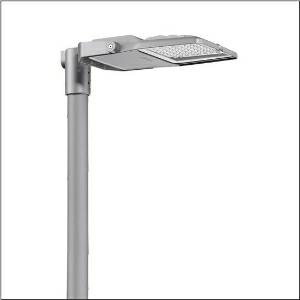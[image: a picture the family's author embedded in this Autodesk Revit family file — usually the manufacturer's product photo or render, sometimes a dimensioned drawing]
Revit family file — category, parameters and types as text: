
# Revit family: floodlight_fl_21_mini___pl43_5xa7776b4a3a_9af8
name_source: partatom
category: Lighting Fixtures
units: mm (PartAtom-declared; Revit-internal decimal feet)

## family parameters
Cut with Voids When Loaded = No
Host = Face
Light Source = No
Part Type = Normal
Room Calculation Point = No
Round Connector Dimension = Use Diameter
Shared = No

## types (1)
- --- (1 x LED, 6650 lm, 45.7 W, 4000K)
    Apparent Load = 46 VA
    CIE Flux Codes = 27 78 99 100 100
    Color Rendering = 70
    Color Temperature = 4000K
    Default Elevation = 1800 mm
    Description = Floodlight FL 21 mini, floodlight, primary light control with lens, of PMMA, primary optical cover: protective disc, of toughened safety glass, transparent, light distribution: PL43, light emission: direct distribution, installation type: surface-mounted, LED, High Power LED, rated luminous flux: 6.650lm, luminous efficacy: 146lm/W, light colour: 740, colour temperature: 4000K, control gear: D4iSmart Interface (Zhaga), control: overheat protection, constant luminous flux control, time-dependent luminous flux control, flexible luminous flux parameterisation, pre-setting: logarithmic dimming characteristic, with terminal, 6-pole, mains connection: 220..240V, AC, 50/60Hz, start of lifetime: 46W, end of service life: 48W, reduction: 22W, mast bracket, of diecast aluminium, powder-coated, SITECO metallic grey (DB 702S), corrosivity category C5 mid according to DIN EN ISO 12944, suitable for swimming pools, chlorine-resistant, sealing non-destructively replaceable, mast bracket, of steel, galvanised, powder-coated, SITECO metallic grey (DB 702S), Smart Interface below and above, protection rating (complete): IP66, insulation class (complete): insulation class II (safety insulation), certification: CE, ENEC, VDE, protection symbol: D, impact resistance: IK08, permissible operating ambient temperature: -40..+40°C, permissible operating ambient temperature for outdoor applications: -40..+50°C, standard: DIN EN 12944, LABS conformity tested according to VDMA 24364:2018-05, packaging unit: 1 piece

Light Distribution: PL43
    Height = 70 mm
    Lamp = 1 x LED
    Lamp Light Flux = 6650 lm
    Lamp Power = 45.7 W
    Lamp count = 1
    Length = 485 mm
    Luminous efficacy = 146 lm/W
    Manufacturer = Siteco
    ModVariant = No
    Model = 5XA7776B4A3A
    Number of Poles = 1
    OnlyDefault = Yes
    Power Factor = 1
    Product Name = Floodlight FL 21 mini | PL43
    Product group = floodlight | pylon annexe
    ProductGroupID = 6201
    Protection Class = Protection class II
    Protection Degree = IP 66
    RLX_Detail_Level = 1
    RLX_Emergency_Light_Flux = 0 lm
    RLX_Emergency_Type = 0
    RLX_Emergency_Type_DB = No
    RlxData = <blob elided: 100817 chars, md5=57cc50f0>
    Socket = socket
    Standby Power = 0 W
    System Light Flux = 6650 lm
    System Power = 46 W
    Type Comments = factory setting: luminous flux: 100 % | dim-lin: 254 | 463 mA
    Type Image = l_1007125.jpg
    URL = http://relux.com
    VarID = @adj_099197
    Voltage = 0 V
    Weight = 0.00 kg
    Width = 337 mm

## geometry (parser evidence)
native form markers: Blend x4, Sweep x15
no freeform markers — native parametric forms only
